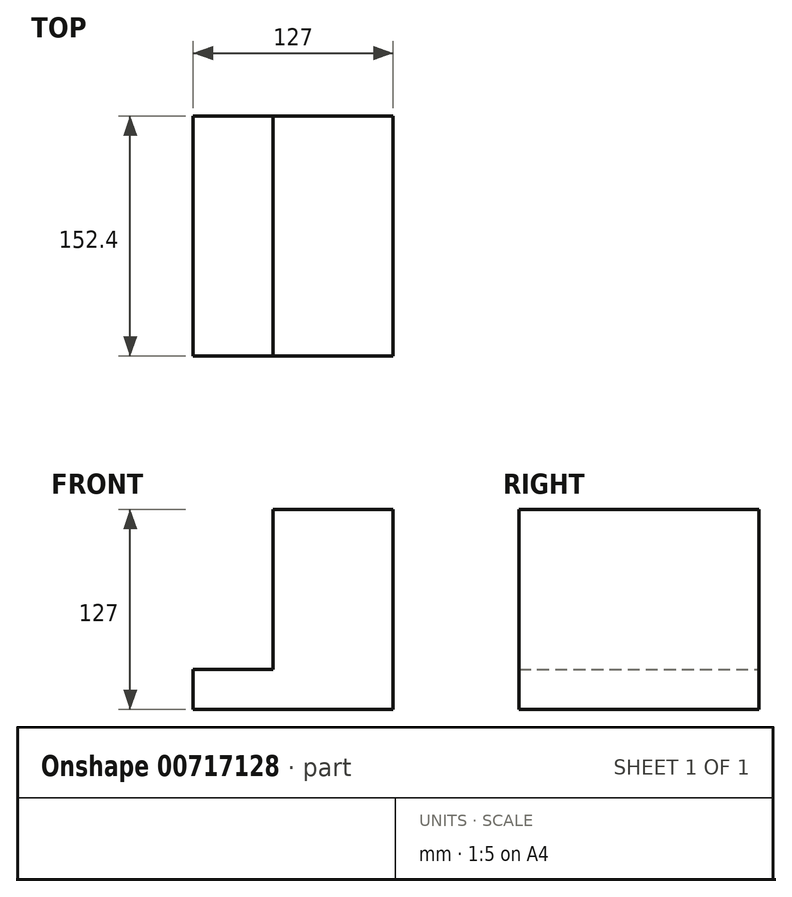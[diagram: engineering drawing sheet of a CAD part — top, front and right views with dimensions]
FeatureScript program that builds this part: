
annotation { "Feature Type Name" : "Feature", "Feature Type Description" : "" }
export const myFeature = defineFeature(function(context is Context, id is Id, definition is map)
    precondition{}
    {
        {
            var Q0;
            Q0=qCreatedBy(makeId("Front.planeOp"),FACE);
            var sketch = newSketch(context, id + "F0", { "sketchPlane" : qUnion([Q0])});
            skLineSegment(sketch, "E0", {"start": v(-73.14, -54.51) * mm, "end": v(-22.34, -54.51) * mm});
            skLineSegment(sketch, "E1", {"start": v(-22.34, -54.51) * mm, "end": v(-22.34, 47.09) * mm});
            skLineSegment(sketch, "E2", {"start": v(-22.34, 47.09) * mm, "end": v(53.86, 47.09) * mm});
            skLineSegment(sketch, "E3", {"start": v(53.86, 47.09) * mm, "end": v(53.86, -79.91) * mm});
            skLineSegment(sketch, "E4", {"start": v(53.86, -79.91) * mm, "end": v(-73.14, -79.91) * mm});
            skLineSegment(sketch, "E5", {"start": v(-73.14, -79.91) * mm, "end": v(-73.14, -54.51) * mm});
            skSolve(sketch);
        }
        {
            var Q0;
            Q0=makeQuery(id+"F0.imprint","IMPRINT",FACE,{"disambiguationData":[TD([[makeQuery(id+"F0.imprint","IMPRINT",EDGE,{"derivedFrom":sQuery(id+"F0.wireOp",EDGE,"E0")}),-1.0]])]});
            extrude(context, id + "F1", {"entities" : qUnion([Q0]), "depth" : 152.4 * mm, "offsetDistance" : 25.4 * mm});
        }
    });
